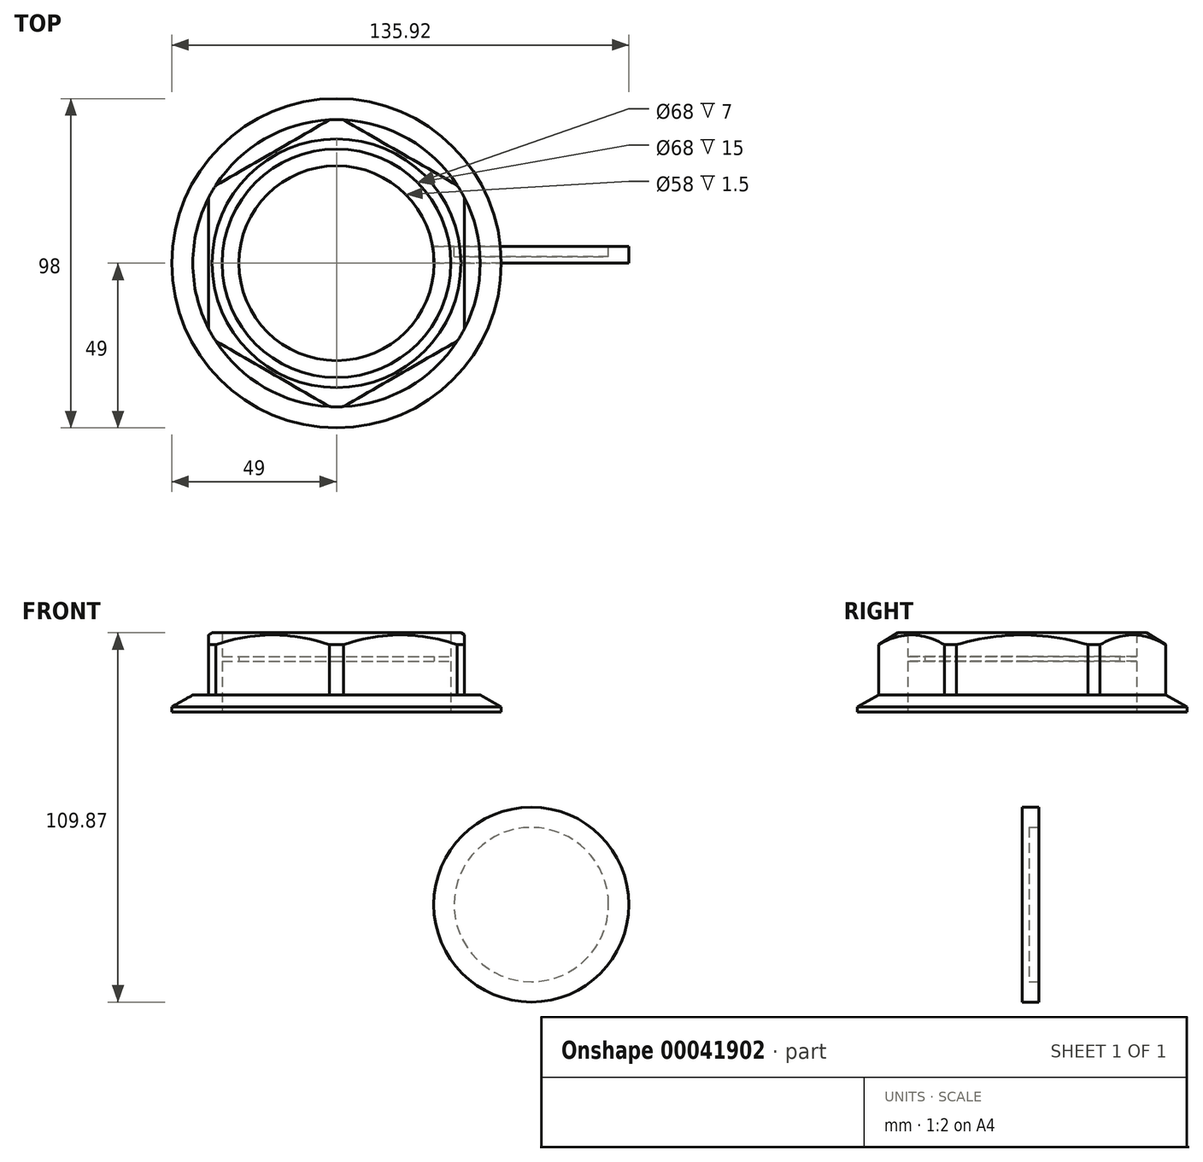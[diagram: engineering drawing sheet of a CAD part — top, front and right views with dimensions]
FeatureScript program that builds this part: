
annotation { "Feature Type Name" : "Feature", "Feature Type Description" : "" }
export const myFeature = defineFeature(function(context is Context, id is Id, definition is map)
    precondition{}
    {
        {
            var Q0;
            Q0=qCreatedBy(makeId("Front.planeOp"),FACE);
            var sketch = newSketch(context, id + "F0", { "sketchPlane" : qUnion([Q0])});
            skLineSegment(sketch, "E0", {"start": v(-34, 0) * mm, "end": v(-49, 0) * mm});
            skLineSegment(sketch, "E1", {"start": v(-49, 0) * mm, "end": v(-49, 1.5) * mm});
            skLineSegment(sketch, "E2", {"start": v(-49, 1.5) * mm, "end": v(-42.73, 5) * mm});
            skLineSegment(sketch, "E3", {"start": v(-34, 23.5) * mm, "end": v(-34, 16.5) * mm});
            skLineSegment(sketch, "E4", {"start": v(-34, 16.5) * mm, "end": v(-29, 16.5) * mm});
            skLineSegment(sketch, "E5", {"start": v(-29, 16.5) * mm, "end": v(-29, 15) * mm});
            skLineSegment(sketch, "E6", {"start": v(-29, 15) * mm, "end": v(-34, 15) * mm});
            skLineSegment(sketch, "E7", {"start": v(-34, 15) * mm, "end": v(-34, 0) * mm});
            skLineSegment(sketch, "E8", {"start": v(-34, 23.5) * mm, "end": v(-37, 23.5) * mm});
            skLineSegment(sketch, "E9", {"start": v(-37, 23.5) * mm, "end": v(-42.73, 20) * mm});
            skLineSegment(sketch, "E10", {"start": v(-42.73, 20) * mm, "end": v(-42.73, 5) * mm});
            skLineSegment(sketch, "E11", {"start": v(0, 0) * mm, "end": v(0, 20.78) * mm, "construction": true});
            skSolve(sketch);
        }
        {
            var Q0;
            Q0=makeQuery(id+"F0.imprint","IMPRINT",FACE,{"disambiguationData":[TD([[makeQuery(id+"F0.imprint","IMPRINT",EDGE,{"derivedFrom":sQuery(id+"F0.wireOp",EDGE,"E0")}),-1.0]])]});
            var Q1;
            Q1=sQuery(id+"F0.wireOp",EDGE,"E11");
            revolve(context, id + "F1", {"entities" : qUnion([Q0]), "axis" : qUnion([Q1]), "revolveType" : RevolveType.FULL});
        }
        {
            var Q0;
            Q0=qCreatedBy(makeId("Top.planeOp"),FACE);
            var sketch = newSketch(context, id + "F2", { "sketchPlane" : qUnion([Q0])});
            skCircle(sketch, "E12", {"center": v(0, 0) * mm, "radius": 48 * mm, "construction": true});
            skArc(sketch, "E13", {"start": v(-38, 21.79) * mm, "mid": v(-43.8, 0) * mm, "end": v(-38, -21.79) * mm});
            skLineSegment(sketch, "E14", {"start": v(-38, 21.79) * mm, "end": v(-38, -21.79) * mm});
            skArc(sketch, "E15.1.0", {"start": v(-37.87, -22.02) * mm, "mid": v(-21.9, -37.93) * mm, "end": v(-0.13, -43.8) * mm});
            skLineSegment(sketch, "E15.1.1", {"start": v(-37.87, -22.02) * mm, "end": v(-0.13, -43.8) * mm});
            skArc(sketch, "E15.2.0", {"start": v(0.13, -43.8) * mm, "mid": v(21.9, -37.93) * mm, "end": v(37.87, -22.02) * mm});
            skLineSegment(sketch, "E15.2.1", {"start": v(0.13, -43.8) * mm, "end": v(37.87, -22.02) * mm});
            skArc(sketch, "E15.3.0", {"start": v(38, -21.79) * mm, "mid": v(43.8, 0) * mm, "end": v(38, 21.79) * mm});
            skLineSegment(sketch, "E15.3.1", {"start": v(38, -21.79) * mm, "end": v(38, 21.79) * mm});
            skArc(sketch, "E15.4.0", {"start": v(37.87, 22.02) * mm, "mid": v(21.9, 37.93) * mm, "end": v(0.13, 43.8) * mm});
            skLineSegment(sketch, "E15.4.1", {"start": v(37.87, 22.02) * mm, "end": v(0.13, 43.8) * mm});
            skArc(sketch, "E15.5.0", {"start": v(-0.13, 43.8) * mm, "mid": v(-21.9, 37.93) * mm, "end": v(-37.87, 22.02) * mm});
            skLineSegment(sketch, "E15.5.1", {"start": v(-0.13, 43.8) * mm, "end": v(-37.87, 22.02) * mm});
            skSolve(sketch);
        }
        {
            var Q0;
            Q0 = qSketchRegion(id + "F2", true);
            extrude(context, id + "F3", {"entities" : qUnion([Q0]), "operationType" : NewBodyOperationType.REMOVE, "depth" : 29.3 * mm, "hasSecondDirection" : true, "secondDirectionOppositeDirection" : false, "secondDirectionDepth" : 5 * mm});
        }
        {
            var Q0;
            Q0=qCreatedBy(makeId("Front.planeOp"),FACE);
            var sketch = newSketch(context, id + "F4", { "sketchPlane" : qUnion([Q0])});
            skCircle(sketch, "E16", {"center": v(57.92, -57.37) * mm, "radius": 29 * mm});
            skCircle(sketch, "E17", {"center": v(57.92, -57.37) * mm, "radius": 25 * mm});
            skSolve(sketch);
        }
        {
            var Q0;
            Q0=makeQuery(id+"F4.imprint","IMPRINT",FACE,{"disambiguationData":[TD([[makeQuery(id+"F4.imprint","IMPRINT",EDGE,{"derivedFrom":sQuery(id+"F4.wireOp",EDGE,"E16")}),1.0]])]});
            var Q1;
            Q1=makeQuery(id+"F4.imprint","IMPRINT",FACE,{"disambiguationData":[TD([[makeQuery(id+"F4.imprint","IMPRINT",EDGE,{"derivedFrom":sQuery(id+"F4.wireOp",EDGE,"E17")}),1.0]])]});
            extrude(context, id + "F5", {"entities" : qUnion([Q0, Q1]), "oppositeDirection" : true, "depth" : 5 * mm, "offsetDistance" : 25 * mm});
        }
        {
            var Q0;
            Q0 = qSketchRegion(id + "F4", true);
            var Q1;
            Q1=makeQuery(id+"F5.opExtrude","CAP_FACE",FACE,{"disambiguationData":[OSD([sQuery(id+"F4.wireOp",EDGE,"E16")])],"isStart":true});
            extrude(context, id + "F6", {"entities" : qUnion([Q0, Q1]), "operationType" : NewBodyOperationType.ADD, "oppositeDirection" : true, "depth" : 3 * mm, "offsetDistance" : 25 * mm});
        }
        {
            var Q0;
            Q0=makeQuery(id+"F5.opExtrude","CAP_FACE",FACE,{"disambiguationData":[OSD([sQuery(id+"F4.wireOp",EDGE,"E16")])],"isStart":false});
            var sketch = newSketch(context, id + "F7", { "sketchPlane" : qUnion([Q0])});
            skCircle(sketch, "E18", {"center": v(-57.92, -57.37) * mm, "radius": 22.96 * mm});
            skSolve(sketch);
        }
        {
            var Q0;
            Q0 = qSketchRegion(id + "F7", true);
            extrude(context, id + "F8", {"entities" : qUnion([Q0]), "operationType" : NewBodyOperationType.REMOVE, "oppositeDirection" : true, "depth" : 3 * mm, "offsetDistance" : 25 * mm});
        }
    });
